# Revit family: Ceiling-Fan_VCDD-040C_Carnes
name_source: partatom
category: Mechanical Equipment
revit_build: Autodesk Revit Architecture 2012 (Build: 20110309_2315)
units: mm (PartAtom-declared; Revit-internal decimal feet)

## types (1)
- Ceiling-Fan_VCDD-040C_Carnes
    04 CSI = 23 37 13
    95 CSI = 15850
    Assembly Code = D3040200
    Box Depth = 0' - 11 3/4"
    Box Size = 21-1/2 x 12-1/4
    Catalog URL = http://www.carnes.com
    Description = Ceiling Ventilators
    Duct Connector = 4-1/2 x 18
    Grill Depth = 0' - 0 3/8"
    Grill Size = 23-1/4 x 14
    Housing = Aluminum-Carnes-Spun-Brushed
    IOM Instructions URL = http://www.carnes.com
    Manufacturer = CARNES COMPANY
    Manufacturer Fax = 608-845-6470
    Model = VCDD 040C
    Parts List URL = http://www.carnes.com
    Product Page URL = http://www.carnes.com
    URL = http://www.carnes.com
    Warranty URL = http://www.carnes.com
    ecoScorecard Product Page = http://ecoscorecard.com

## geometry (parser evidence)
native form markers: Blend x6, Sweep x1
no freeform markers — native parametric forms only
